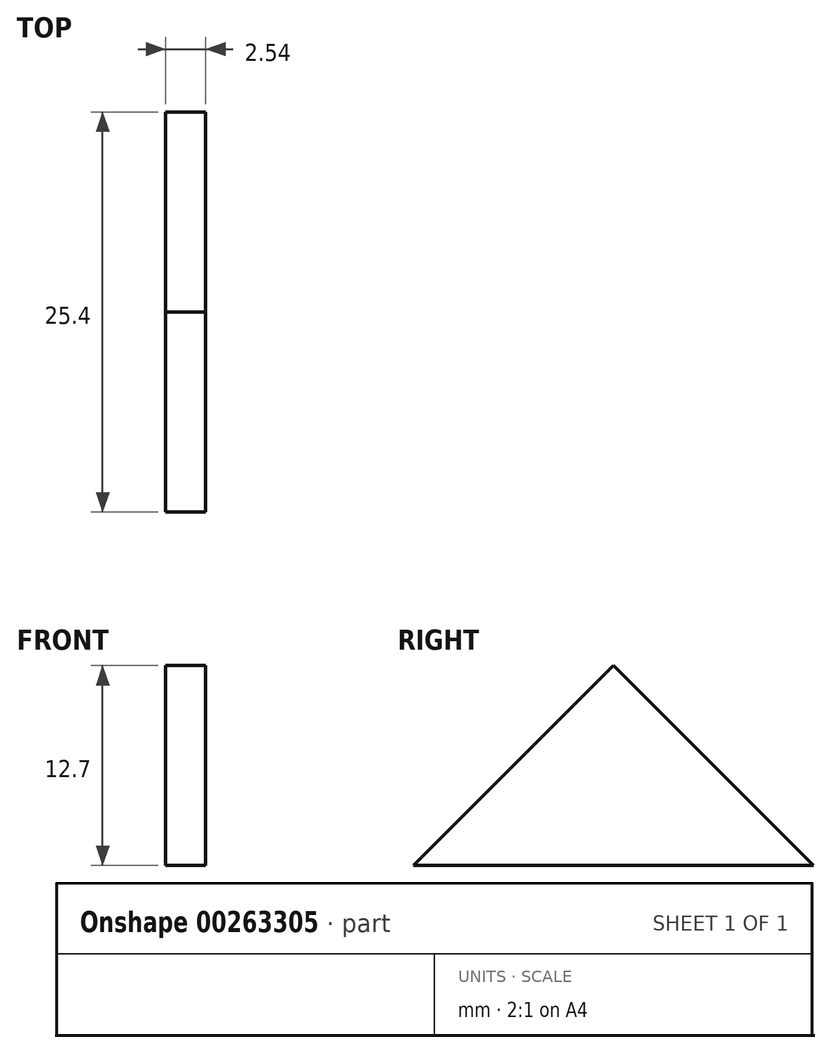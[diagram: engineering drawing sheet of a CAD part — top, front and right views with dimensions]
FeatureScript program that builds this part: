
annotation { "Feature Type Name" : "Feature", "Feature Type Description" : "" }
export const myFeature = defineFeature(function(context is Context, id is Id, definition is map)
    precondition{}
    {
        {
            var Q0;
            Q0=qCreatedBy(makeId("Right.planeOp"),FACE);
            var sketch = newSketch(context, id + "F0", { "sketchPlane" : qUnion([Q0])});
            skLineSegment(sketch, "E0", {"start": v(-38.25, -15.95) * mm, "end": v(88.75, -15.95) * mm});
            skLineSegment(sketch, "E1", {"start": v(25.25, -15.95) * mm, "end": v(25.25, 47.55) * mm});
            skLineSegment(sketch, "E2", {"start": v(-38.25, -15.95) * mm, "end": v(25.25, 47.55) * mm});
            skLineSegment(sketch, "E3", {"start": v(88.75, -15.95) * mm, "end": v(25.25, 47.55) * mm});
            skLineSegment(sketch, "E4", {"start": v(25.25, 47.55) * mm, "end": v(25.25, 34.85) * mm});
            skLineSegment(sketch, "E5", {"start": v(25.25, 34.85) * mm, "end": v(12.55, 34.85) * mm});
            skLineSegment(sketch, "E6", {"start": v(12.55, 34.85) * mm, "end": v(37.95, 34.85) * mm});
            skLineSegment(sketch, "E7", {"start": v(37.95, 34.85) * mm, "end": v(33.46, 30.36) * mm});
            skLineSegment(sketch, "E8", {"start": v(88.75, -15.95) * mm, "end": v(84.26, -20.44) * mm});
            skLineSegment(sketch, "E9", {"start": v(84.26, -20.44) * mm, "end": v(28.97, 34.85) * mm});
            skLineSegment(sketch, "E10", {"start": v(79.77, -15.95) * mm, "end": v(28.97, 34.85) * mm});
            skPoint(sketch, "E11.endSnap0", {"position": v(18.9, 34.85) * mm});
            skLineSegment(sketch, "E12", {"start": v(12.55, 34.85) * mm, "end": v(17.04, 30.36) * mm});
            skLineSegment(sketch, "E13", {"start": v(-38.25, -15.95) * mm, "end": v(-33.76, -20.44) * mm});
            skLineSegment(sketch, "E14", {"start": v(17.04, 30.36) * mm, "end": v(21.53, 34.85) * mm});
            skLineSegment(sketch, "E15", {"start": v(21.53, 34.85) * mm, "end": v(-33.76, -20.44) * mm});
            skLineSegment(sketch, "E16", {"start": v(-33.76, -20.44) * mm, "end": v(-29.27, -15.95) * mm});
            skSolve(sketch);
        }
        {
            var Q0;
            {var subQ1=sQuery(id+"F0.wireOp",EDGE,"E1");Q0=makeQuery(id+"F0.imprint","IMPRINT",FACE,{"disambiguationData":[TD([[makeQuery(id+"F0.imprint","IMPRINT",EDGE,{"derivedFrom":subQ1}),1.0]])]});}
            var Q1;
            {var subQ1=sQuery(id+"F0.wireOp",EDGE,"E1");Q1=makeQuery(id+"F0.imprint","IMPRINT",FACE,{"disambiguationData":[TD([[makeQuery(id+"F0.imprint","IMPRINT",EDGE,{"derivedFrom":subQ1}),-1.0]])]});}
            extrude(context, id + "F1", {"entities" : qUnion([Q0, Q1]), "endBound" : BoundingType.SYMMETRIC, "depth" : 2.54 * mm});
        }
    });
